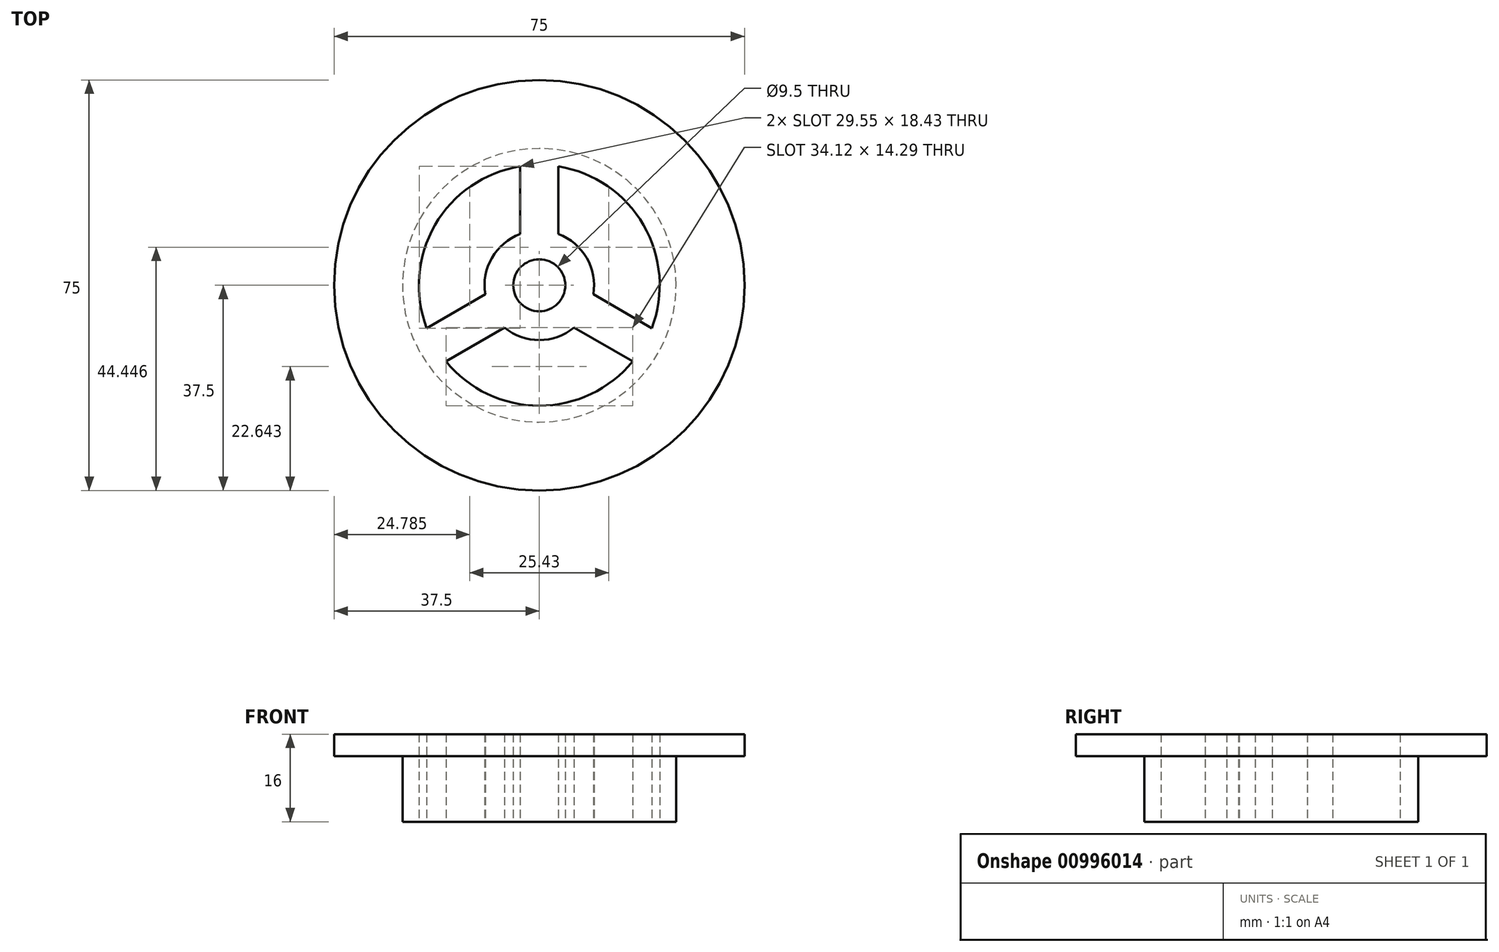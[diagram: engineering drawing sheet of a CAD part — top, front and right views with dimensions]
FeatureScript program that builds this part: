
annotation { "Feature Type Name" : "Feature", "Feature Type Description" : "" }
export const myFeature = defineFeature(function(context is Context, id is Id, definition is map)
    precondition{}
    {
        {
            var Q0;
            Q0=qCreatedBy(makeId("Top.planeOp"),FACE);
            var sketch = newSketch(context, id + "F0", { "sketchPlane" : qUnion([Q0])});
            skCircle(sketch, "E0", {"center": v(0, 0) * mm, "radius": 4.75 * mm});
            skCircle(sketch, "E1", {"center": v(0, 0) * mm, "radius": 25 * mm});
            skLineSegment(sketch, "E2", {"start": v(-3.5, 24.75) * mm, "end": v(-3.5, 9.37) * mm});
            skLineSegment(sketch, "E3", {"start": v(3.5, 9.37) * mm, "end": v(3.5, 24.75) * mm});
            skPoint(sketch, "E4", {"position": v(0, 25) * mm});
            skLineSegment(sketch, "E5", {"start": v(-9.86, -1.65) * mm, "end": v(-23.19, -9.35) * mm});
            skLineSegment(sketch, "E6", {"start": v(-19.69, -15.4) * mm, "end": v(-6.36, -7.71) * mm});
            skLineSegment(sketch, "E7", {"start": v(6.36, -7.71) * mm, "end": v(19.69, -15.4) * mm});
            skLineSegment(sketch, "E8", {"start": v(23.19, -9.35) * mm, "end": v(9.86, -1.65) * mm});
            skLineSegment(sketch, "E9", {"start": v(-9.86, -1.65) * mm, "end": v(-6.36, -7.71) * mm, "construction": true});
            skLineSegment(sketch, "E10", {"start": v(9.86, -1.65) * mm, "end": v(6.36, -7.71) * mm, "construction": true});
            skLineSegment(sketch, "E11", {"start": v(-8.11, -4.68) * mm, "end": v(-8.28, -4.78) * mm});
            skLineSegment(sketch, "E12", {"start": v(8.11, -4.68) * mm, "end": v(8.46, -4.88) * mm});
            skLineSegment(sketch, "E13", {"start": v(0, -49.96) * mm, "end": v(0, 59.07) * mm, "construction": true});
            skLineSegment(sketch, "E14", {"start": v(-36.9, 21.3) * mm, "end": v(34.56, -19.95) * mm, "construction": true});
            skLineSegment(sketch, "E15", {"start": v(-52.6, -30.37) * mm, "end": v(42.48, 24.53) * mm, "construction": true});
            skCircle(sketch, "E16", {"center": v(0, 0) * mm, "radius": 10 * mm});
            skCircle(sketch, "E17", {"center": v(0, 0) * mm, "radius": 37.5 * mm});
            skCircle(sketch, "E18", {"center": v(0, 0) * mm, "radius": 22 * mm});
            skSolve(sketch);
        }
        {
            var Q0;
            Q0=makeQuery(id+"F0.imprint","IMPRINT",FACE,{"disambiguationData":[TD([[makeQuery(id+"F0.imprint","IMPRINT",EDGE,{"derivedFrom":sQuery(id+"F0.wireOp",EDGE,"E17")}),1.0]])]});
            var Q1;
            {var subQ0=sQuery(id+"F0.wireOp",EDGE,"E2");Q1=makeQuery(id+"F0.imprint","IMPRINT",FACE,{"disambiguationData":[TD([[makeQuery(id+"F0.imprint","IMPRINT",EDGE,{"derivedFrom":subQ0}),1.0]])]});}
            var Q2;
            {var subQ1=sQuery(id+"F0.wireOp",EDGE,"E7");Q2=makeQuery(id+"F0.imprint","IMPRINT",FACE,{"disambiguationData":[TD([[makeQuery(id+"F0.imprint","IMPRINT",EDGE,{"derivedFrom":subQ1}),1.0]])]});}
            var Q3;
            {var subQ0=sQuery(id+"F0.wireOp",EDGE,"E5");Q3=makeQuery(id+"F0.imprint","IMPRINT",FACE,{"disambiguationData":[TD([[makeQuery(id+"F0.imprint","IMPRINT",EDGE,{"derivedFrom":subQ0}),1.0]])]});}
            var Q4;
            Q4=makeQuery(id+"F0.imprint","IMPRINT",FACE,{"disambiguationData":[TD([[makeQuery(id+"F0.imprint","IMPRINT",EDGE,{"derivedFrom":sQuery(id+"F0.wireOp",EDGE,"E0")}),-1.0]])]});
            var Q5;
            {var subQ0=sQuery(id+"F0.wireOp",EDGE,"E3");var subQ1=sQuery(id+"F0.wireOp",EDGE,"E1");var subQ2=makeQuery(id+"F0.imprint","INTERSECT",VERTEX,{"derivedFrom":[subQ1,subQ0]});Q5=makeQuery(id+"F0.imprint","IMPRINT",FACE,{"disambiguationData":[TD([[makeQuery(id+"F0.imprint","IMPRINT",EDGE,{"disambiguationData":[TD([[subQ2,1.0]])],"derivedFrom":subQ1}),1.0]])]});}
            var Q6;
            {var subQ0=sQuery(id+"F0.wireOp",EDGE,"E6");var subQ1=sQuery(id+"F0.wireOp",EDGE,"E1");var subQ2=makeQuery(id+"F0.imprint","INTERSECT",VERTEX,{"derivedFrom":[subQ1,subQ0]});Q6=makeQuery(id+"F0.imprint","IMPRINT",FACE,{"disambiguationData":[TD([[makeQuery(id+"F0.imprint","IMPRINT",EDGE,{"disambiguationData":[TD([[subQ2,-1.0]])],"derivedFrom":subQ1}),1.0]])]});}
            var Q7;
            {var subQ0=sQuery(id+"F0.wireOp",EDGE,"E2");var subQ1=sQuery(id+"F0.wireOp",EDGE,"E1");var subQ2=makeQuery(id+"F0.imprint","INTERSECT",VERTEX,{"derivedFrom":[subQ1,subQ0]});Q7=makeQuery(id+"F0.imprint","IMPRINT",FACE,{"disambiguationData":[TD([[makeQuery(id+"F0.imprint","IMPRINT",EDGE,{"disambiguationData":[TD([[subQ2,-1.0]])],"derivedFrom":subQ1}),1.0]])]});}
            extrude(context, id + "F1", {"entities" : qUnion([Q0, Q1, Q2, Q3, Q4, Q5, Q6, Q7]), "depth" : 4 * mm, "offsetDistance" : 25 * mm});
        }
        {
            var Q0;
            {var subQ0=sQuery(id+"F0.wireOp",EDGE,"E3");var subQ1=sQuery(id+"F0.wireOp",EDGE,"E1");var subQ2=makeQuery(id+"F0.imprint","INTERSECT",VERTEX,{"derivedFrom":[subQ1,subQ0]});Q0=makeQuery(id+"F0.imprint","IMPRINT",FACE,{"disambiguationData":[TD([[makeQuery(id+"F0.imprint","IMPRINT",EDGE,{"disambiguationData":[TD([[subQ2,1.0]])],"derivedFrom":subQ1}),1.0]])]});}
            var Q1;
            {var subQ0=sQuery(id+"F0.wireOp",EDGE,"E2");var subQ1=sQuery(id+"F0.wireOp",EDGE,"E1");var subQ2=makeQuery(id+"F0.imprint","INTERSECT",VERTEX,{"derivedFrom":[subQ1,subQ0]});Q1=makeQuery(id+"F0.imprint","IMPRINT",FACE,{"disambiguationData":[TD([[makeQuery(id+"F0.imprint","IMPRINT",EDGE,{"disambiguationData":[TD([[subQ2,1.0]])],"derivedFrom":subQ1}),1.0]])]});}
            var Q2;
            {var subQ0=sQuery(id+"F0.wireOp",EDGE,"E2");var subQ1=sQuery(id+"F0.wireOp",EDGE,"E1");var subQ2=makeQuery(id+"F0.imprint","INTERSECT",VERTEX,{"derivedFrom":[subQ1,subQ0]});Q2=makeQuery(id+"F0.imprint","IMPRINT",FACE,{"disambiguationData":[TD([[makeQuery(id+"F0.imprint","IMPRINT",EDGE,{"disambiguationData":[TD([[subQ2,-1.0]])],"derivedFrom":subQ1}),1.0]])]});}
            var Q3;
            {var subQ0=sQuery(id+"F0.wireOp",EDGE,"E5");var subQ1=sQuery(id+"F0.wireOp",EDGE,"E1");var subQ2=makeQuery(id+"F0.imprint","INTERSECT",VERTEX,{"derivedFrom":[subQ1,subQ0]});Q3=makeQuery(id+"F0.imprint","IMPRINT",FACE,{"disambiguationData":[TD([[makeQuery(id+"F0.imprint","IMPRINT",EDGE,{"disambiguationData":[TD([[subQ2,-1.0]])],"derivedFrom":subQ1}),1.0]])]});}
            var Q4;
            {var subQ0=sQuery(id+"F0.wireOp",EDGE,"E6");var subQ1=sQuery(id+"F0.wireOp",EDGE,"E1");var subQ2=makeQuery(id+"F0.imprint","INTERSECT",VERTEX,{"derivedFrom":[subQ1,subQ0]});Q4=makeQuery(id+"F0.imprint","IMPRINT",FACE,{"disambiguationData":[TD([[makeQuery(id+"F0.imprint","IMPRINT",EDGE,{"disambiguationData":[TD([[subQ2,-1.0]])],"derivedFrom":subQ1}),1.0]])]});}
            var Q5;
            {var subQ0=sQuery(id+"F0.wireOp",EDGE,"E7");var subQ1=sQuery(id+"F0.wireOp",EDGE,"E1");var subQ2=makeQuery(id+"F0.imprint","INTERSECT",VERTEX,{"derivedFrom":[subQ1,subQ0]});Q5=makeQuery(id+"F0.imprint","IMPRINT",FACE,{"disambiguationData":[TD([[makeQuery(id+"F0.imprint","IMPRINT",EDGE,{"disambiguationData":[TD([[subQ2,-1.0]])],"derivedFrom":subQ1}),1.0]])]});}
            var Q6;
            {var subQ0=sQuery(id+"F0.wireOp",EDGE,"E16");var subQ1=sQuery(id+"F0.wireOp",EDGE,"E2");var subQ2=makeQuery(id+"F0.imprint","INTERSECT",VERTEX,{"derivedFrom":[subQ1,subQ0]});Q6=makeQuery(id+"F0.imprint","IMPRINT",FACE,{"disambiguationData":[TD([[makeQuery(id+"F0.imprint","IMPRINT",EDGE,{"disambiguationData":[TD([[subQ2,1.0]])],"derivedFrom":subQ1}),1.0]])]});}
            var Q7;
            {var subQ0=sQuery(id+"F0.wireOp",EDGE,"E16");var subQ1=sQuery(id+"F0.wireOp",EDGE,"E7");var subQ2=makeQuery(id+"F0.imprint","INTERSECT",VERTEX,{"derivedFrom":[subQ1,subQ0]});Q7=makeQuery(id+"F0.imprint","IMPRINT",FACE,{"disambiguationData":[TD([[makeQuery(id+"F0.imprint","IMPRINT",EDGE,{"disambiguationData":[TD([[subQ2,-1.0]])],"derivedFrom":subQ1}),1.0]])]});}
            var Q8;
            {var subQ0=sQuery(id+"F0.wireOp",EDGE,"E16");var subQ1=sQuery(id+"F0.wireOp",EDGE,"E5");var subQ2=makeQuery(id+"F0.imprint","INTERSECT",VERTEX,{"derivedFrom":[subQ1,subQ0]});Q8=makeQuery(id+"F0.imprint","IMPRINT",FACE,{"disambiguationData":[TD([[makeQuery(id+"F0.imprint","IMPRINT",EDGE,{"disambiguationData":[TD([[subQ2,-1.0]])],"derivedFrom":subQ1}),1.0]])]});}
            var Q9;
            Q9=makeQuery(id+"F0.imprint","IMPRINT",FACE,{"disambiguationData":[TD([[makeQuery(id+"F0.imprint","IMPRINT",EDGE,{"derivedFrom":sQuery(id+"F0.wireOp",EDGE,"E0")}),-1.0]])]});
            extrude(context, id + "F2", {"entities" : qUnion([Q0, Q1, Q2, Q3, Q4, Q5, Q6, Q7, Q8, Q9]), "operationType" : NewBodyOperationType.ADD, "depth" : -12 * mm, "offsetDistance" : 25 * mm});
        }
    });
